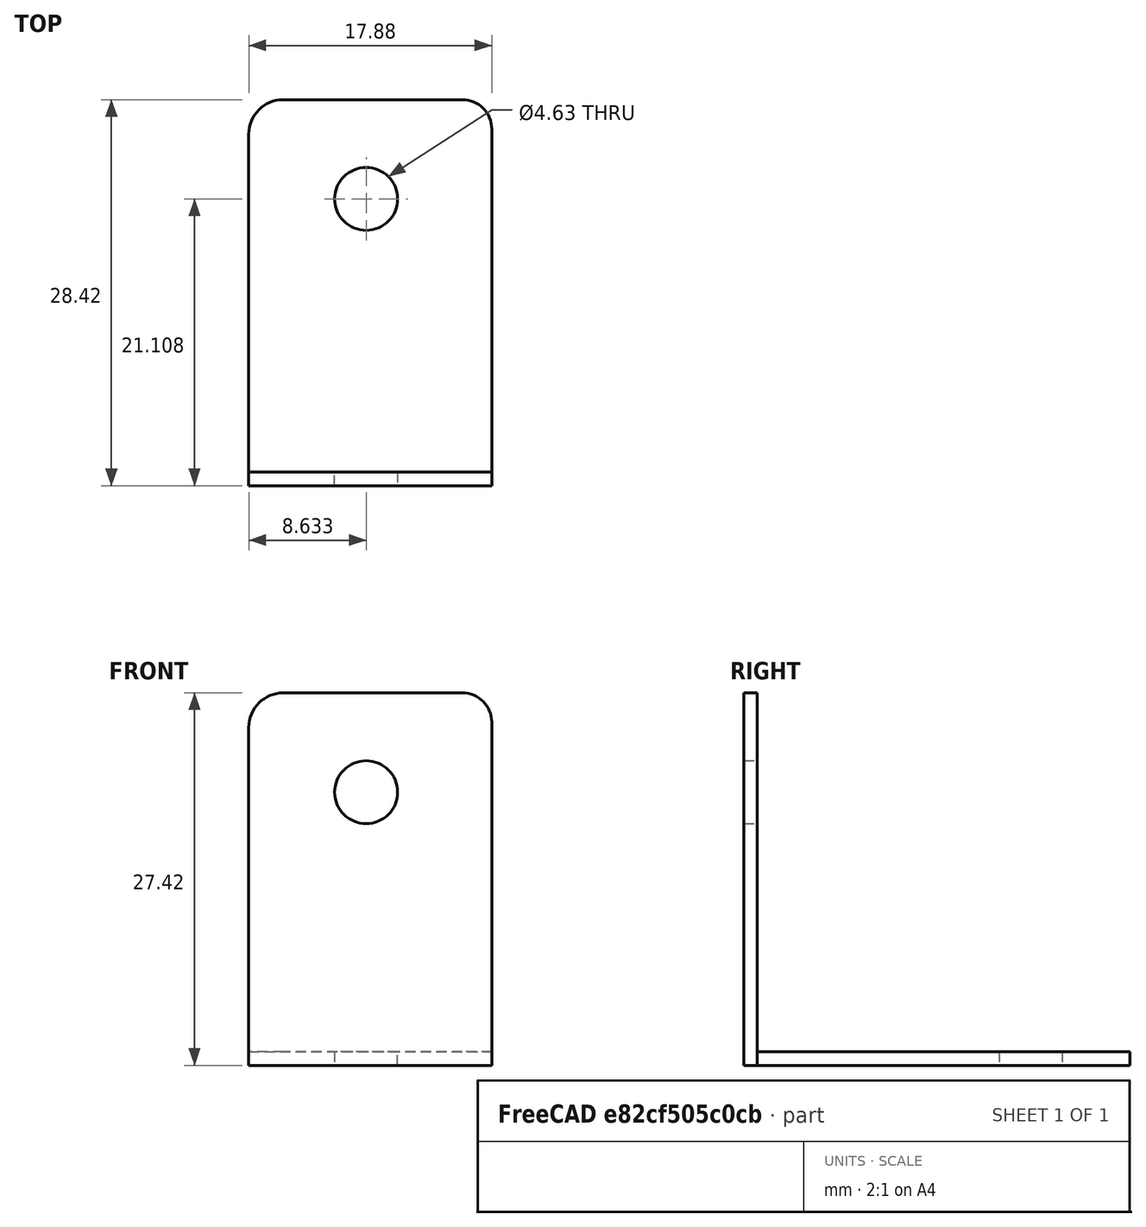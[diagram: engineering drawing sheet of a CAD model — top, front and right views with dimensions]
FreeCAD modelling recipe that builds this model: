
FCSTD DOCUMENT  (FreeCAD 0.19R24291 (Git))
Label: escuadras_rueda_loca
License: All rights reserved
LicenseURL: http://en.wikipedia.org/wiki/All_rights_reserved
objects: TechDraw::DrawProjGroupItem×3, Sketcher::SketchObject×2, PartDesign::Pad×2, PartDesign::Body×2, App::LinkGroup×1, TechDraw::DrawSVGTemplate×1, TechDraw::DrawProjGroup×1, TechDraw::DrawPage×1
note: 8 computed .brp shape members not serialized (recipe doc carries the construction recipe); baked Part::Feature solids carry a one-line shape summary decoded from their .brp

FEATURE [Sketcher::SketchObject] Sketch
  FullyConstrained = false
  MapMode = 5
  Support = -> [XY_Plane]
  sketch-geometry (7):
    g0: LineSegment StartX=-8.06452 StartY=0 StartZ=0 EndX=9.82406 EndY=0 EndZ=0
    g1: LineSegment StartX=9.82406 StartY=0 StartZ=0 EndX=9.82406 EndY=25.2473 EndZ=0
    g2: LineSegment StartX=7.652 StartY=27.4194 StartZ=0 EndX=-5.53469 EndY=27.4194 EndZ=0
    g3: LineSegment StartX=-8.06452 StartY=24.8895 StartZ=0 EndX=-8.06452 EndY=0 EndZ=0
    g4: ArcOfCircle CenterX=-5.53469 CenterY=24.8895 CenterZ=0 NormalX=0 NormalY=0 NormalZ=1 AngleXU=0 Radius=2.52983 StartAngle=1.5708 EndAngle=3.14159
    g5: ArcOfCircle CenterX=7.652 CenterY=25.2473 CenterZ=0 NormalX=0 NormalY=0 NormalZ=1 AngleXU=0 Radius=2.17205 StartAngle=0 EndAngle=1.5708
    g6: Circle CenterX=0.573308 CenterY=20.1084 CenterZ=0 NormalX=0 NormalY=0 NormalZ=1 AngleXU=0 Radius=2.31699
  constraints (11):
    c: Coincident(g0,g1)
    c: Coincident(g3,g0)
    c: Horizontal(g0)
    c: Horizontal(g2)
    c: Vertical(g1)
    c: Vertical(g3)
    c: PointOnObject(g0,g-1)
    c: Tangent(g2,g4) = -1.5708
    c: Tangent(g3,g4) = -1.5708
    c: Tangent(g1,g5) = -1.5708
    c: Tangent(g2,g5) = -1.5708
FEATURE [PartDesign::Pad] Pad
  Direction = (1,1,1)
  Length = 1
  Length2 = 100
  Profile = -> Sketch
  Type = 0
FEATURE [PartDesign::Body] Body  label="abajo"
  Group = -> [Sketch,Pad]
  Origin = -> Origin
  Tip = -> Pad
FEATURE [Sketcher::SketchObject] Sketch001
  FullyConstrained = false
  MapMode = 5
  Support = -> [XY_Plane001]
  sketch-geometry (7):
    g0: LineSegment StartX=-8.06452 StartY=0 StartZ=0 EndX=9.82406 EndY=0 EndZ=0
    g1: LineSegment StartX=9.82406 StartY=0 StartZ=0 EndX=9.82406 EndY=25.2473 EndZ=0
    g2: LineSegment StartX=7.652 StartY=27.4194 StartZ=0 EndX=-5.53469 EndY=27.4194 EndZ=0
    g3: LineSegment StartX=-8.06452 StartY=24.8895 StartZ=0 EndX=-8.06452 EndY=0 EndZ=0
    g4: ArcOfCircle CenterX=-5.53469 CenterY=24.8895 CenterZ=0 NormalX=0 NormalY=0 NormalZ=1 AngleXU=0 Radius=2.52983 StartAngle=1.5708 EndAngle=3.14159
    g5: ArcOfCircle CenterX=7.652 CenterY=25.2473 CenterZ=0 NormalX=0 NormalY=0 NormalZ=1 AngleXU=0 Radius=2.17205 StartAngle=0 EndAngle=1.5708
    g6: Circle CenterX=0.573308 CenterY=20.1084 CenterZ=0 NormalX=0 NormalY=0 NormalZ=1 AngleXU=0 Radius=2.31699
  constraints (11):
    c: Coincident(g0,g1)
    c: Coincident(g3,g0)
    c: Horizontal(g0)
    c: Horizontal(g2)
    c: Vertical(g1)
    c: Vertical(g3)
    c: PointOnObject(g0,g-1)
    c: Tangent(g2,g4) = -1.5708
    c: Tangent(g3,g4) = -1.5708
    c: Tangent(g1,g5) = -1.5708
    c: Tangent(g2,g5) = -1.5708
FEATURE [PartDesign::Pad] Pad001
  Direction = (1,1,1)
  Length = 1
  Length2 = 100
  Profile = -> Sketch001
  Type = 0
FEATURE [PartDesign::Body] Body001  label="arriba"
  Group = -> [Sketch001,Pad001]
  Origin = -> Origin001
  Placement = pos=(0,0,0) rot=(1,0,0;1.5708rad)
  Tip = -> Pad001
FEATURE [App::LinkGroup] LinkGroup  label="escuadra_final"
  ElementList = -> [Body001,Body]
  LinkMode = 0
FEATURE [TechDraw::DrawSVGTemplate] Template
  EditableTexts = Designed_by_Name=Los legendarios; Drawing_number=Drawing number; FC-Date=Date; FC-SC=1:1; FC-SH=Sheet; FC-Title=Escuadra individual; Subtitle=Subtitle; Weight=Weight
  Height = 210
  Orientation = 1
  Width = 297
FEATURE [TechDraw::DrawProjGroupItem] ProjItem  label="Front"
  CoarseView = false
  Direction = (0,0,1)
  Focus = 100
  HardHidden = false
  IsoCount = 0
  IsoHidden = false
  IsoVisible = false
  LockPosition = true
  Perspective = false
  Rotation = 0
  RotationVector = (1,0,0)
  ScaleType = 2
  SeamHidden = false
  SeamVisible = true
  SmoothHidden = false
  SmoothVisible = true
  Type = 0
  X = 0
  XDirection = (1,0,0)
  XSource = -> [LinkGroup]
  Y = 0
FEATURE [TechDraw::DrawProjGroupItem] ProjItem001  label="Left"
  CoarseView = false
  Direction = (-1,0,1e-16)
  Focus = 100
  HardHidden = false
  IsoCount = 0
  IsoHidden = false
  IsoVisible = false
  LockPosition = false
  Perspective = false
  Rotation = 0
  RotationVector = (1,0,0)
  ScaleType = 2
  SeamHidden = false
  SeamVisible = true
  SmoothHidden = false
  SmoothVisible = true
  Type = 1
  X = 42.4194
  XDirection = (1e-16,0,1)
  XSource = -> [LinkGroup]
  Y = 0
FEATURE [TechDraw::DrawProjGroupItem] ProjItem002  label="Top"
  CoarseView = false
  Direction = (0,1,0)
  Focus = 100
  HardHidden = false
  IsoCount = 0
  IsoHidden = false
  IsoVisible = false
  LockPosition = false
  Perspective = false
  Rotation = 0
  RotationVector = (1,0,0)
  ScaleType = 2
  SeamHidden = false
  SeamVisible = true
  SmoothHidden = false
  SmoothVisible = true
  Type = 4
  X = 0
  XDirection = (1,0,0)
  XSource = -> [LinkGroup]
  Y = -43.9194
FEATURE [TechDraw::DrawProjGroup] ProjGroup
  Anchor = -> ProjItem
  AutoDistribute = true
  LockPosition = false
  ProjectionType = 0
  Rotation = 0
  ScaleType = 0
  Views = -> [ProjItem,ProjItem001,ProjItem002]
  X = 115.372
  XSource = -> [LinkGroup]
  Y = 141.497
  spacingX = 15
  spacingY = 15
FEATURE [TechDraw::DrawPage] Page
  KeepUpdated = true
  NextBalloonIndex = 1
  ProjectionType = 0
  Template = -> Template
  Views = -> [ProjGroup]
